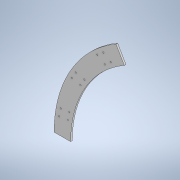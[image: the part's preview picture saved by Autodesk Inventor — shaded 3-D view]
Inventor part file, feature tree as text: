
AUTODESK INVENTOR PART (.ipt)
format: ipt  version: 2020.3 (Build 243373000, 373)  size: 148,992 bytes
history: native  units: mm
features: extrude x3, pattern_circular x1, sketch x1
ambient origin geometry x8: Origin, YZ Plane, XZ Plane, XY Plane, X Axis, Y Axis, Z Axis, Center Point
bodies: Solid1 (feature_tree)
feature tree (5):
  extrude  "Extrusion1"  Depth=10.0mm
  extrude  "Extrusion2"  Depth=4.0mm TaperAngle=0.0deg
  extrude  "Extrusion3"  Depth=10.0mm TaperAngle=0.0deg
  pattern_circular  "Circular Pattern1"  [2 undecoded]
  sketch  "Sketch1"  dims[d0=600.0mm d1=40.0mm d2=4.0mm d3=0.0mm d4=10.0mm d5=0.0mm d6=3.0mm d7=3.0mm d9=270.0mm d11=3.0mm d12=3.0mm d14=270.0mm d16=0.0mm d17=0.0mm d18=90.0mm d19=27.925268mm d21=19.024089mm d22=20.0mm d23=1.396263mm d24=2.094395mm d25=60.0deg]
note: 2 required parameter values undecoded (feature->parameter linkage not recoverable at this tier; creation-order binding heuristic only, values carry confidence <= 0.55)
